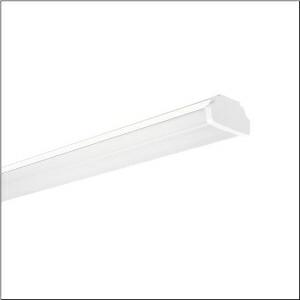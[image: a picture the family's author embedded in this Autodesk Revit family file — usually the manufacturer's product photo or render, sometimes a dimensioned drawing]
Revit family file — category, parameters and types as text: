
# Revit family: modario_31_gen_2_53bm812cv4dxd2_d5c2
name_source: partatom
category: Lighting Fixtures
units: mm (PartAtom-declared; Revit-internal decimal feet)

## family parameters
Cut with Voids When Loaded = No
Host = Face
Light Source = No
Part Type = Normal
Room Calculation Point = No
Round Connector Dimension = Use Diameter
Shared = No

## types (1)
- --- (1 x LED, 13040 lm, 68.5 W, 4000K)
    Apparent Load = 69 VA
    CIE Flux Codes = 47 80 95 93 100
    Color Rendering = 80
    Color Temperature = 4000K
    Default Elevation = 1800 mm
    Description = Modario 31 Gen.2, luminaire insert, of sheet steel, coil coated, white, length: 1.495mm, width: 81mm, height: 82mm, 5x system unit, system units: 299mm, LED rated luminous flux: 13.040lm, light colour: 840, SDCM (Standard Deviation of Colour Matching)MacAdam ≤ 3 SDCM (initial), control gear: ON/OFF Multilumen, CLOi, with plug, 3-pole, with phase selection, mains connection: 220..240V, AC, 50/60Hz, start of lifetime: 69W, end of service life: 82W, through-wiring accessed according to module size, primary optical cover: cover, of PMMA, light emission: direct distribution, primary light characteristic: symmetric, protection rating (complete): IP20, protection rating (LED compartment): IP50, insulation class (complete): insulation class I (protective earthing), certification: CE, ENEC, VDE, UKCA, impact resistance: IK03, permissible ambient temperature for indoor applications: -35..+35°C, corresponds to IFS (International Featured Standards) requirements for safety and quality in the food industry, reducing of maximum allowable ambient temperature of 5°C with ceiling mounting, IP40 when using the optional accessory 5TP9018, packaging unit: 1 piece
    Height = 92 mm
    Lamp = 1 x LED
    Lamp Light Flux = 13040 lm
    Lamp Power = 68.5 W
    Lamp count = 1
    Length = 1495 mm
    Luminous efficacy = 190 lm/W
    Manufacturer = Siteco
    ModVariant = No
    Model = 53BM812CV4DXD2
    Mounting Place = Ceiling
    Mounting Type = Pendant
    Number of Poles = 1
    OnlyDefault = Yes
    Power Factor = 1
    Product Name = Modario 31 Gen.2
    Product group = luminaire insert | ceiling pendant
    ProductGroupID = 901
    Protection Class = Protection class I
    Protection Degree = IP 20
    RLX_Detail_Level = 1
    RLX_Emergency_Light_Flux = 0 lm
    RLX_Emergency_Type = 0
    RLX_Emergency_Type_DB = No
    RlxData = <blob elided: 40165 chars, md5=21288eb3>
    Socket = socket
    Standby Power = 0 W
    System Light Flux = 13040 lm
    System Power = 69 W
    Type Comments = factory setting: luminous flux: 100 % | (A | C | E) | 161 mA
    Type Image = l_1341886.jpg
    URL = http://relux.com
    VarID = @adj_050753
    Voltage = 0 V
    Weight = 0.00 kg
    Width = 81 mm

## geometry (parser evidence)
native form markers: Blend x4, Sweep x11
no freeform markers — native parametric forms only
